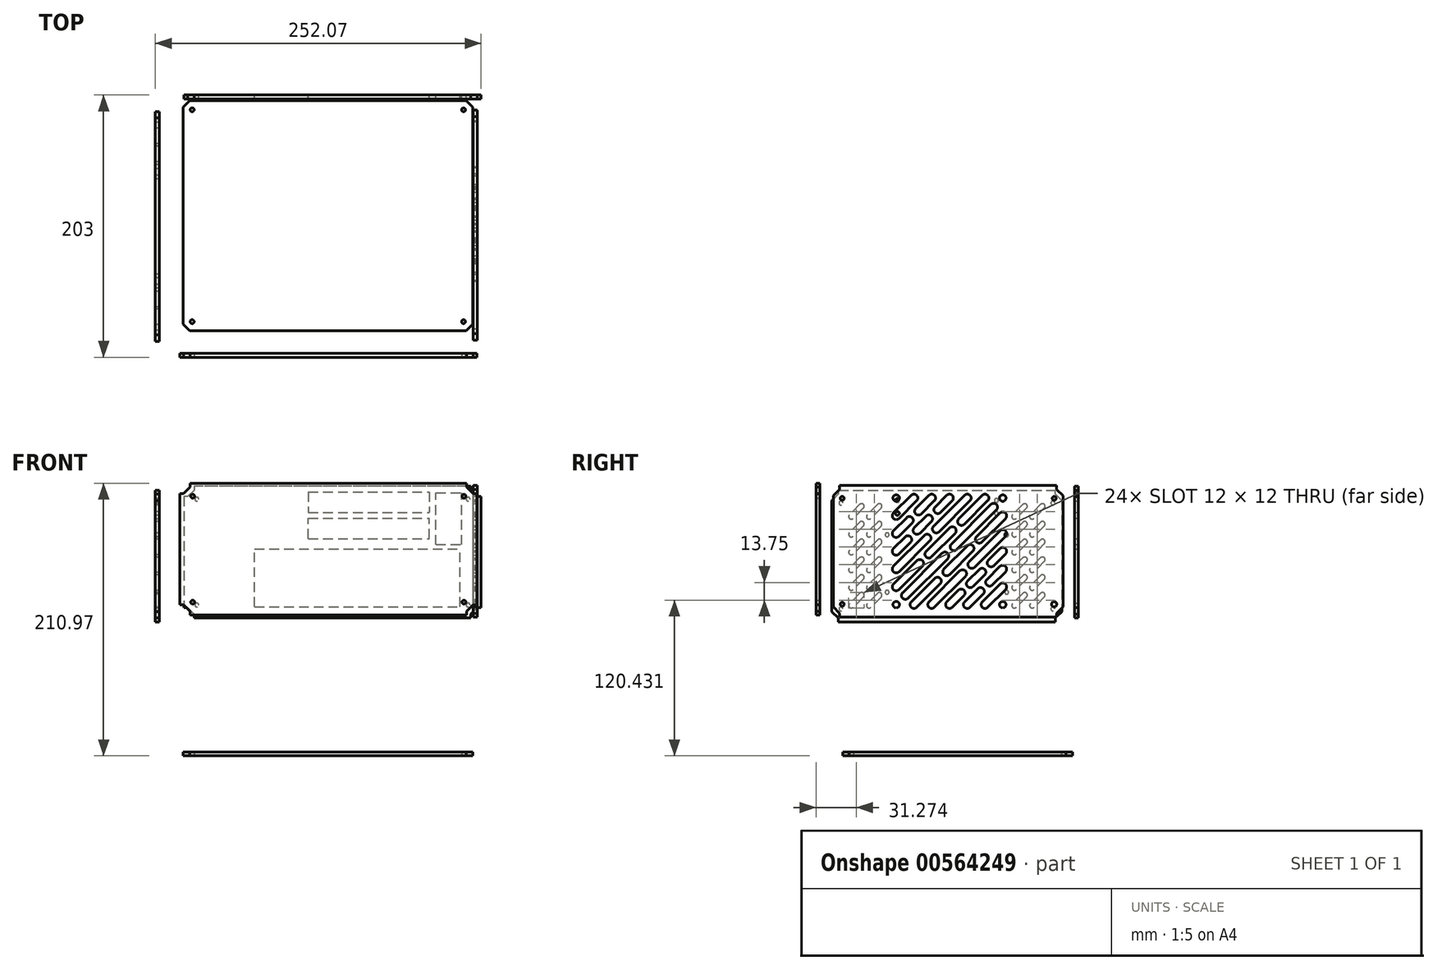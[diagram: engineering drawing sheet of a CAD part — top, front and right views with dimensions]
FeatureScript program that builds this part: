
annotation { "Feature Type Name" : "Feature", "Feature Type Description" : "" }
export const myFeature = defineFeature(function(context is Context, id is Id, definition is map)
    precondition{}
    {
        {
            var Q0;
            Q0=qCreatedBy(makeId("Front.planeOp"),FACE);
            cPlane(context, id + "F0", {"entities" : qUnion([Q0]), "cplaneType" : CPlaneType.OFFSET, "offset" : 80 * mm, "width" : 150 * mm, "height" : 150 * mm});
        }
        {
            var Q0;
            Q0=qCreatedBy(id+"F0.planeOp",FACE);
            var sketch = newSketch(context, id + "F1", { "sketchPlane" : qUnion([Q0])});
            skLineSegment(sketch, "E0.bottom", {"start": v(-107.2, 58.97) * mm, "end": v(122.8, 58.97) * mm});
            skLineSegment(sketch, "E0.top", {"start": v(-107.2, -43.03) * mm, "end": v(122.8, -43.03) * mm});
            skLineSegment(sketch, "E0.left", {"start": v(-107.2, 58.97) * mm, "end": v(-107.2, -43.03) * mm});
            skLineSegment(sketch, "E0.right", {"start": v(122.8, 58.97) * mm, "end": v(122.8, -43.03) * mm});
            skLineSegment(sketch, "E1", {"start": v(114.8, 58.97) * mm, "end": v(114.8, 55.97) * mm});
            skLineSegment(sketch, "E2", {"start": v(114.8, 55.97) * mm, "end": v(119.8, 50.97) * mm});
            skLineSegment(sketch, "E3", {"start": v(119.8, 50.97) * mm, "end": v(122.8, 50.97) * mm});
            skLineSegment(sketch, "E4", {"start": v(122.8, -35.03) * mm, "end": v(119.8, -35.03) * mm});
            skLineSegment(sketch, "E5", {"start": v(119.8, -35.03) * mm, "end": v(114.8, -40.03) * mm});
            skLineSegment(sketch, "E6", {"start": v(114.8, -40.03) * mm, "end": v(114.8, -43.03) * mm});
            skLineSegment(sketch, "E7", {"start": v(-107.2, -35.03) * mm, "end": v(-104.2, -35.03) * mm});
            skLineSegment(sketch, "E8", {"start": v(-104.2, -35.03) * mm, "end": v(-99.2, -40.03) * mm});
            skLineSegment(sketch, "E9", {"start": v(-99.2, -40.03) * mm, "end": v(-99.2, -43.03) * mm});
            skLineSegment(sketch, "E10", {"start": v(-107.2, 50.97) * mm, "end": v(-104.2, 50.97) * mm});
            skLineSegment(sketch, "E11", {"start": v(-104.2, 50.97) * mm, "end": v(-99.2, 55.97) * mm});
            skLineSegment(sketch, "E12", {"start": v(-99.2, 55.97) * mm, "end": v(-99.2, 58.97) * mm});
            skLineSegment(sketch, "E13", {"start": v(-107.2, 48.97) * mm, "end": v(-97.2, 48.97) * mm, "construction": true});
            skCircle(sketch, "E14", {"center": v(-97.2, 48.97) * mm, "radius": 1.5 * mm});
            skLineSegment(sketch, "E15", {"start": v(-107.2, -33.03) * mm, "end": v(-97.2, -33.03) * mm, "construction": true});
            skLineSegment(sketch, "E16", {"start": v(122.8, 48.97) * mm, "end": v(112.8, 48.97) * mm, "construction": true});
            skLineSegment(sketch, "E17", {"start": v(122.8, -33.03) * mm, "end": v(112.8, -33.03) * mm, "construction": true});
            skCircle(sketch, "E18", {"center": v(112.8, -33.03) * mm, "radius": 1.5 * mm});
            skCircle(sketch, "E19", {"center": v(112.8, 48.97) * mm, "radius": 1.5 * mm});
            skCircle(sketch, "E20", {"center": v(-97.2, -33.03) * mm, "radius": 1.5 * mm});
            skSolve(sketch);
        }
        {
            var Q0;
            {var subQ2=sQuery(id+"F1.wireOp",EDGE,"E1");Q0=makeQuery(id+"F1.imprint","IMPRINT",FACE,{"disambiguationData":[TD([[makeQuery(id+"F1.imprint","IMPRINT",EDGE,{"derivedFrom":subQ2}),-1.0]])]});}
            extrude(context, id + "F2", {"entities" : qUnion([Q0]), "depth" : 3 * mm, "offsetDistance" : 25 * mm});
        }
        {
            var Q0;
            Q0=qCreatedBy(makeId("Right.planeOp"),FACE);
            cPlane(context, id + "F3", {"entities" : qUnion([Q0]), "cplaneType" : CPlaneType.OFFSET, "offset" : 120 * mm, "width" : 150 * mm, "height" : 150 * mm});
        }
        {
            var Q0;
            Q0=qCreatedBy(id+"F3.planeOp",FACE);
            var sketch = newSketch(context, id + "F4", { "sketchPlane" : qUnion([Q0])});
            skLineSegment(sketch, "E21.bottom", {"start": v(-69.71, 57.33) * mm, "end": v(108.29, 57.33) * mm});
            skLineSegment(sketch, "E21.top", {"start": v(-69.71, -44.67) * mm, "end": v(108.29, -44.67) * mm});
            skLineSegment(sketch, "E21.left", {"start": v(-69.71, 57.33) * mm, "end": v(-69.71, -44.67) * mm});
            skLineSegment(sketch, "E21.right", {"start": v(108.29, 57.33) * mm, "end": v(108.29, -44.67) * mm});
            skLineSegment(sketch, "E22", {"start": v(-64.71, 57.33) * mm, "end": v(-64.71, 54.33) * mm});
            skLineSegment(sketch, "E23", {"start": v(-64.71, 54.33) * mm, "end": v(-69.71, 49.33) * mm});
            skLineSegment(sketch, "E24", {"start": v(-69.71, -36.67) * mm, "end": v(-64.71, -41.67) * mm});
            skLineSegment(sketch, "E25", {"start": v(-64.71, -41.67) * mm, "end": v(-64.71, -44.67) * mm});
            skLineSegment(sketch, "E26", {"start": v(103.29, 57.33) * mm, "end": v(103.29, 54.33) * mm});
            skLineSegment(sketch, "E27", {"start": v(103.29, 54.33) * mm, "end": v(108.29, 49.33) * mm});
            skLineSegment(sketch, "E28", {"start": v(108.29, -36.67) * mm, "end": v(103.29, -41.67) * mm});
            skLineSegment(sketch, "E29", {"start": v(103.29, -41.67) * mm, "end": v(103.29, -44.67) * mm});
            skLineSegment(sketch, "E30", {"start": v(-69.71, 47.33) * mm, "end": v(-62.71, 47.33) * mm, "construction": true});
            skCircle(sketch, "E31", {"center": v(-62.71, 47.33) * mm, "radius": 1.5 * mm});
            skLineSegment(sketch, "E32", {"start": v(-69.71, -34.67) * mm, "end": v(-62.71, -34.67) * mm, "construction": true});
            skCircle(sketch, "E33", {"center": v(-62.71, -34.67) * mm, "radius": 1.5 * mm});
            skLineSegment(sketch, "E34", {"start": v(108.29, -34.67) * mm, "end": v(101.29, -34.67) * mm, "construction": true});
            skCircle(sketch, "E35", {"center": v(101.29, -34.67) * mm, "radius": 2.05 * mm});
            skLineSegment(sketch, "E36", {"start": v(108.29, 47.33) * mm, "end": v(101.29, 47.33) * mm, "construction": true});
            skCircle(sketch, "E37", {"center": v(101.29, 47.33) * mm, "radius": 1.5 * mm});
            skSolve(sketch);
        }
        {
            var Q0;
            {var subQ4=sQuery(id+"F4.wireOp",EDGE,"E22");Q0=makeQuery(id+"F4.imprint","IMPRINT",FACE,{"disambiguationData":[TD([[makeQuery(id+"F4.imprint","IMPRINT",EDGE,{"derivedFrom":subQ4}),1.0]])]});}
            extrude(context, id + "F5", {"entities" : qUnion([Q0]), "depth" : 3 * mm, "offsetDistance" : 25 * mm});
        }
        {
            var Q0;
            Q0=qCreatedBy(makeId("Front.planeOp"),FACE);
            cPlane(context, id + "F6", {"entities" : qUnion([Q0]), "cplaneType" : CPlaneType.OFFSET, "offset" : 120 * mm, "oppositeDirection" : true, "width" : 150 * mm, "height" : 150 * mm});
        }
        {
            var Q0;
            Q0=qCreatedBy(id+"F6.planeOp",FACE);
            var sketch = newSketch(context, id + "F7", { "sketchPlane" : qUnion([Q0])});
            skLineSegment(sketch, "E38.bottom", {"start": v(126.07, 56.7) * mm, "end": v(-103.93, 56.7) * mm});
            skLineSegment(sketch, "E38.top", {"start": v(126.07, -45.3) * mm, "end": v(-103.93, -45.3) * mm});
            skLineSegment(sketch, "E38.left", {"start": v(126.07, 56.7) * mm, "end": v(126.07, -45.3) * mm});
            skLineSegment(sketch, "E38.right", {"start": v(-103.93, 56.7) * mm, "end": v(-103.93, -45.3) * mm});
            skLineSegment(sketch, "E39", {"start": v(126.07, 48.7) * mm, "end": v(123.07, 48.7) * mm});
            skLineSegment(sketch, "E40", {"start": v(123.07, 48.7) * mm, "end": v(118.07, 53.7) * mm});
            skLineSegment(sketch, "E41", {"start": v(118.07, 53.7) * mm, "end": v(118.07, 56.7) * mm});
            skLineSegment(sketch, "E42", {"start": v(-95.93, 56.7) * mm, "end": v(-95.93, 53.7) * mm});
            skLineSegment(sketch, "E43", {"start": v(-95.93, 53.7) * mm, "end": v(-100.93, 48.7) * mm});
            skLineSegment(sketch, "E44", {"start": v(-100.93, 48.7) * mm, "end": v(-103.93, 48.7) * mm});
            skLineSegment(sketch, "E45", {"start": v(-95.93, -45.3) * mm, "end": v(-95.93, -42.3) * mm});
            skLineSegment(sketch, "E46", {"start": v(-95.93, -42.3) * mm, "end": v(-100.93, -37.3) * mm});
            skLineSegment(sketch, "E47", {"start": v(-100.93, -37.3) * mm, "end": v(-103.93, -37.3) * mm});
            skLineSegment(sketch, "E48", {"start": v(126.07, -37.3) * mm, "end": v(123.07, -37.3) * mm});
            skLineSegment(sketch, "E49", {"start": v(123.07, -37.3) * mm, "end": v(118.07, -42.3) * mm});
            skLineSegment(sketch, "E50", {"start": v(118.07, -42.3) * mm, "end": v(118.07, -45.3) * mm});
            skLineSegment(sketch, "E51", {"start": v(-103.93, 46.7) * mm, "end": v(-93.93, 46.7) * mm, "construction": true});
            skCircle(sketch, "E52", {"center": v(-93.93, 46.7) * mm, "radius": 1.5 * mm});
            skLineSegment(sketch, "E53", {"start": v(-103.93, -35.3) * mm, "end": v(-93.93, -35.3) * mm, "construction": true});
            skCircle(sketch, "E54", {"center": v(-93.93, -35.3) * mm, "radius": 1.5 * mm});
            skLineSegment(sketch, "E55", {"start": v(126.07, 46.7) * mm, "end": v(116.07, 46.7) * mm, "construction": true});
            skCircle(sketch, "E56", {"center": v(116.07, 46.7) * mm, "radius": 1.5 * mm});
            skLineSegment(sketch, "E57", {"start": v(126.07, -35.3) * mm, "end": v(116.07, -35.3) * mm, "construction": true});
            skCircle(sketch, "E58", {"center": v(116.07, -35.3) * mm, "radius": 1.5 * mm});
            skSolve(sketch);
        }
        {
            var Q0;
            {var subQ2=sQuery(id+"F7.wireOp",EDGE,"E39");Q0=makeQuery(id+"F7.imprint","IMPRINT",FACE,{"disambiguationData":[TD([[makeQuery(id+"F7.imprint","IMPRINT",EDGE,{"derivedFrom":subQ2}),1.0]])]});}
            extrude(context, id + "F8", {"entities" : qUnion([Q0]), "depth" : 3 * mm, "offsetDistance" : 25 * mm});
        }
        {
            var Q0;
            Q0=makeQuery(id+"F8.opExtrude","CAP_FACE",FACE,{"disambiguationData":[OSD([sQuery(id+"F7.wireOp",EDGE,"E38.bottom"),sQuery(id+"F7.wireOp",EDGE,"E38.top"),sQuery(id+"F7.wireOp",EDGE,"E38.left"),sQuery(id+"F7.wireOp",EDGE,"E38.right")])],"isStart":true});
            var sketch = newSketch(context, id + "F9", { "sketchPlane" : qUnion([Q0])});
            skLineSegment(sketch, "E59", {"start": v(-107.07, -34.3) * mm, "end": v(62.93, -34.3) * mm, "construction": true});
            skLineSegment(sketch, "E60", {"start": v(-107.07, -34.3) * mm, "end": v(-107.07, -45.3) * mm, "construction": true});
            skLineSegment(sketch, "E61.bottom", {"start": v(-109.67, 8.1) * mm, "end": v(49.33, 8.1) * mm});
            skLineSegment(sketch, "E61.top", {"start": v(-109.67, -36.6) * mm, "end": v(49.33, -36.6) * mm});
            skLineSegment(sketch, "E61.left", {"start": v(-109.67, 8.1) * mm, "end": v(-109.67, -36.6) * mm});
            skLineSegment(sketch, "E61.right", {"start": v(49.33, 8.1) * mm, "end": v(49.33, -36.6) * mm});
            skLineSegment(sketch, "E62.bottom", {"start": v(-86.07, 32) * mm, "end": v(7.63, 32) * mm});
            skLineSegment(sketch, "E62.top", {"start": v(-86.07, 16.1) * mm, "end": v(7.63, 16.1) * mm});
            skLineSegment(sketch, "E62.left", {"start": v(-86.07, 32) * mm, "end": v(-86.07, 16.1) * mm});
            skLineSegment(sketch, "E62.right", {"start": v(7.63, 32) * mm, "end": v(7.63, 16.1) * mm});
            skLineSegment(sketch, "E63", {"start": v(-86.07, 32) * mm, "end": v(-86.07, 36.4) * mm, "construction": true});
            skLineSegment(sketch, "E64.bottom", {"start": v(-86.07, 36.4) * mm, "end": v(7.63, 36.4) * mm});
            skLineSegment(sketch, "E64.top", {"start": v(-86.07, 52.3) * mm, "end": v(7.63, 52.3) * mm});
            skLineSegment(sketch, "E64.left", {"start": v(-86.07, 36.4) * mm, "end": v(-86.07, 52.3) * mm});
            skLineSegment(sketch, "E64.right", {"start": v(7.63, 36.4) * mm, "end": v(7.63, 52.3) * mm});
            skLineSegment(sketch, "E65.bottom", {"start": v(-111.07, 51.6) * mm, "end": v(-91.07, 51.6) * mm});
            skLineSegment(sketch, "E65.top", {"start": v(-111.07, 11.6) * mm, "end": v(-91.07, 11.6) * mm});
            skLineSegment(sketch, "E65.left", {"start": v(-111.07, 51.6) * mm, "end": v(-111.07, 11.6) * mm});
            skLineSegment(sketch, "E65.right", {"start": v(-91.07, 51.6) * mm, "end": v(-91.07, 11.6) * mm});
            skLineSegment(sketch, "E66", {"start": v(-86.07, 16.1) * mm, "end": v(-91.07, 16.1) * mm, "construction": true});
            skSolve(sketch);
        }
        {
            var Q0;
            Q0 = qSketchRegion(id + "F9", true);
            extrude(context, id + "F10", {"entities" : qUnion([Q0]), "operationType" : NewBodyOperationType.REMOVE, "oppositeDirection" : true, "depth" : 25 * mm, "offsetDistance" : 25 * mm});
        }
        {
            var Q0;
            Q0=makeQuery(id+"F5.opExtrude","CAP_FACE",FACE,{"disambiguationData":[OSD([sQuery(id+"F4.wireOp",EDGE,"E21.bottom"),sQuery(id+"F4.wireOp",EDGE,"E21.top"),sQuery(id+"F4.wireOp",EDGE,"E21.left"),sQuery(id+"F4.wireOp",EDGE,"E21.right")])],"isStart":false});
            var sketch = newSketch(context, id + "F11", { "sketchPlane" : qUnion([Q0])});
            skLineSegment(sketch, "E67.bottom", {"start": v(-20.96, 47.58) * mm, "end": v(61.54, 47.58) * mm, "construction": true});
            skLineSegment(sketch, "E67.top", {"start": v(-20.96, -34.92) * mm, "end": v(61.54, -34.92) * mm, "construction": true});
            skLineSegment(sketch, "E67.left", {"start": v(-20.96, 47.58) * mm, "end": v(-20.96, -34.92) * mm, "construction": true});
            skLineSegment(sketch, "E67.right", {"start": v(61.54, 47.58) * mm, "end": v(61.54, -34.92) * mm, "construction": true});
            skLineSegment(sketch, "E68", {"start": v(-20.96, 33.83) * mm, "end": v(-7.21, 47.58) * mm, "construction": true});
            skLineSegment(sketch, "E69", {"start": v(-20.96, 20.08) * mm, "end": v(-10.75, 30.3) * mm, "construction": true});
            skLineSegment(sketch, "E70", {"start": v(-20.96, 6.33) * mm, "end": v(-11.93, 15.36) * mm, "construction": true});
            skLineSegment(sketch, "E71", {"start": v(-20.96, -7.42) * mm, "end": v(3, 16.54) * mm, "construction": true});
            skLineSegment(sketch, "E72", {"start": v(-20.96, -21.17) * mm, "end": v(-2.76, -2.97) * mm, "construction": true});
            skLineSegment(sketch, "E73", {"start": v(-20.96, -34.92) * mm, "end": v(-13.9, -27.85) * mm, "construction": true});
            skArc(sketch, "E74.0.startCap", {"start": v(-18.84, 31.7) * mm, "mid": v(-23.08, 31.7) * mm, "end": v(-23.08, 35.95) * mm});
            skArc(sketch, "E74.0.endCap", {"start": v(-9.33, 49.7) * mm, "mid": v(-5.1, 49.7) * mm, "end": v(-5.1, 45.46) * mm});
            skLineSegment(sketch, "E74.0.left", {"start": v(-23.08, 35.95) * mm, "end": v(-9.33, 49.7) * mm});
            skLineSegment(sketch, "E74.0.right", {"start": v(-18.84, 31.7) * mm, "end": v(-5.1, 45.46) * mm});
            skLineSegment(sketch, "E75", {"start": v(-10.75, 30.3) * mm, "end": v(-3.68, 37.36) * mm, "construction": true});
            skLineSegment(sketch, "E76", {"start": v(-3.68, 37.36) * mm, "end": v(6.54, 47.58) * mm, "construction": true});
            skLineSegment(sketch, "E77", {"start": v(-20.96, -34.92) * mm, "end": v(-20.96, -44.67) * mm, "construction": true});
            skArc(sketch, "E78.0.startCap", {"start": v(-18.84, 17.96) * mm, "mid": v(-23.08, 17.96) * mm, "end": v(-23.08, 22.2) * mm});
            skArc(sketch, "E78.0.endCap", {"start": v(-12.87, 32.41) * mm, "mid": v(-8.63, 32.41) * mm, "end": v(-8.63, 28.17) * mm});
            skLineSegment(sketch, "E78.0.left", {"start": v(-23.08, 22.2) * mm, "end": v(-12.87, 32.41) * mm});
            skLineSegment(sketch, "E78.0.right", {"start": v(-18.84, 17.96) * mm, "end": v(-8.63, 28.17) * mm});
            skArc(sketch, "E78.1.startCap", {"start": v(-1.56, 35.24) * mm, "mid": v(-5.8, 35.24) * mm, "end": v(-5.8, 39.48) * mm});
            skArc(sketch, "E78.1.endCap", {"start": v(4.42, 49.7) * mm, "mid": v(8.66, 49.7) * mm, "end": v(8.66, 45.46) * mm});
            skLineSegment(sketch, "E78.1.left", {"start": v(-5.8, 39.48) * mm, "end": v(4.42, 49.7) * mm});
            skLineSegment(sketch, "E78.1.right", {"start": v(-1.56, 35.24) * mm, "end": v(8.66, 45.46) * mm});
            skLineSegment(sketch, "E79", {"start": v(-11.93, 15.36) * mm, "end": v(-4.86, 22.43) * mm, "construction": true});
            skLineSegment(sketch, "E80", {"start": v(-4.86, 22.43) * mm, "end": v(4.18, 31.47) * mm, "construction": true});
            skLineSegment(sketch, "E81", {"start": v(4.18, 31.47) * mm, "end": v(11.25, 38.54) * mm, "construction": true});
            skLineSegment(sketch, "E82", {"start": v(11.25, 38.54) * mm, "end": v(20.29, 47.58) * mm, "construction": true});
            skArc(sketch, "E83.0.startCap", {"start": v(-18.84, 4.2) * mm, "mid": v(-23.08, 4.2) * mm, "end": v(-23.08, 8.45) * mm});
            skArc(sketch, "E83.0.endCap", {"start": v(-14.05, 17.48) * mm, "mid": v(-9.8, 17.48) * mm, "end": v(-9.8, 13.24) * mm});
            skLineSegment(sketch, "E83.0.left", {"start": v(-23.08, 8.45) * mm, "end": v(-14.05, 17.48) * mm});
            skLineSegment(sketch, "E83.0.right", {"start": v(-18.84, 4.2) * mm, "end": v(-9.8, 13.24) * mm});
            skArc(sketch, "E83.1.startCap", {"start": v(-2.74, 20.31) * mm, "mid": v(-6.98, 20.31) * mm, "end": v(-6.98, 24.56) * mm});
            skArc(sketch, "E83.1.endCap", {"start": v(2.06, 33.6) * mm, "mid": v(6.3, 33.6) * mm, "end": v(6.3, 29.35) * mm});
            skLineSegment(sketch, "E83.1.left", {"start": v(-6.98, 24.56) * mm, "end": v(2.06, 33.6) * mm});
            skLineSegment(sketch, "E83.1.right", {"start": v(-2.74, 20.31) * mm, "end": v(6.3, 29.35) * mm});
            skArc(sketch, "E83.2.startCap", {"start": v(13.37, 36.42) * mm, "mid": v(9.13, 36.42) * mm, "end": v(9.13, 40.66) * mm});
            skArc(sketch, "E83.2.endCap", {"start": v(18.17, 49.7) * mm, "mid": v(22.4, 49.7) * mm, "end": v(22.4, 45.46) * mm});
            skLineSegment(sketch, "E83.2.left", {"start": v(9.13, 40.66) * mm, "end": v(18.17, 49.7) * mm});
            skLineSegment(sketch, "E83.2.right", {"start": v(13.37, 36.42) * mm, "end": v(22.4, 45.46) * mm});
            skLineSegment(sketch, "E84", {"start": v(3, 16.54) * mm, "end": v(10.07, 23.61) * mm, "construction": true});
            skLineSegment(sketch, "E85", {"start": v(10.07, 23.61) * mm, "end": v(34.04, 47.58) * mm, "construction": true});
            skArc(sketch, "E86.0.startCap", {"start": v(-18.84, -9.54) * mm, "mid": v(-23.08, -9.54) * mm, "end": v(-23.08, -5.3) * mm});
            skArc(sketch, "E86.0.endCap", {"start": v(0.88, 18.66) * mm, "mid": v(5.12, 18.66) * mm, "end": v(5.12, 14.42) * mm});
            skLineSegment(sketch, "E86.0.left", {"start": v(-23.08, -5.3) * mm, "end": v(0.88, 18.66) * mm});
            skLineSegment(sketch, "E86.0.right", {"start": v(-18.84, -9.54) * mm, "end": v(5.12, 14.42) * mm});
            skArc(sketch, "E87.0.startCap", {"start": v(12.2, 21.5) * mm, "mid": v(7.95, 21.5) * mm, "end": v(7.95, 25.73) * mm});
            skArc(sketch, "E87.0.endCap", {"start": v(31.92, 49.7) * mm, "mid": v(36.16, 49.7) * mm, "end": v(36.16, 45.46) * mm});
            skLineSegment(sketch, "E87.0.left", {"start": v(7.95, 25.73) * mm, "end": v(31.92, 49.7) * mm});
            skLineSegment(sketch, "E87.0.right", {"start": v(12.2, 21.5) * mm, "end": v(36.16, 45.46) * mm});
            skLineSegment(sketch, "E88", {"start": v(-2.76, -2.97) * mm, "end": v(4.31, 4.1) * mm, "construction": true});
            skLineSegment(sketch, "E89", {"start": v(4.31, 4.1) * mm, "end": v(22.51, 22.3) * mm, "construction": true});
            skLineSegment(sketch, "E90", {"start": v(22.51, 22.3) * mm, "end": v(29.58, 29.37) * mm, "construction": true});
            skLineSegment(sketch, "E91", {"start": v(29.58, 29.37) * mm, "end": v(47.79, 47.58) * mm, "construction": true});
            skArc(sketch, "E92.0.startCap", {"start": v(-18.84, -23.3) * mm, "mid": v(-23.08, -23.3) * mm, "end": v(-23.08, -19.05) * mm});
            skArc(sketch, "E92.0.endCap", {"start": v(-4.88, -0.85) * mm, "mid": v(-0.64, -0.85) * mm, "end": v(-0.64, -5.1) * mm});
            skLineSegment(sketch, "E92.0.left", {"start": v(-23.08, -19.05) * mm, "end": v(-4.88, -0.85) * mm});
            skLineSegment(sketch, "E92.0.right", {"start": v(-18.84, -23.3) * mm, "end": v(-0.64, -5.1) * mm});
            skArc(sketch, "E92.1.startCap", {"start": v(6.43, 1.98) * mm, "mid": v(2.19, 1.98) * mm, "end": v(2.19, 6.22) * mm});
            skArc(sketch, "E92.1.endCap", {"start": v(20.4, 24.42) * mm, "mid": v(24.63, 24.42) * mm, "end": v(24.63, 20.18) * mm});
            skLineSegment(sketch, "E92.1.left", {"start": v(2.19, 6.22) * mm, "end": v(20.4, 24.42) * mm});
            skLineSegment(sketch, "E92.1.right", {"start": v(6.43, 1.98) * mm, "end": v(24.63, 20.18) * mm});
            skArc(sketch, "E92.2.startCap", {"start": v(31.7, 27.25) * mm, "mid": v(27.46, 27.25) * mm, "end": v(27.46, 31.5) * mm});
            skArc(sketch, "E92.2.endCap", {"start": v(45.67, 49.7) * mm, "mid": v(49.9, 49.7) * mm, "end": v(49.9, 45.46) * mm});
            skLineSegment(sketch, "E92.2.left", {"start": v(27.46, 31.5) * mm, "end": v(45.67, 49.7) * mm});
            skLineSegment(sketch, "E92.2.right", {"start": v(31.7, 27.25) * mm, "end": v(49.9, 45.46) * mm});
            skLineSegment(sketch, "E93", {"start": v(-13.9, -27.85) * mm, "end": v(16.75, 2.8) * mm, "construction": true});
            skLineSegment(sketch, "E94", {"start": v(54.47, 40.5) * mm, "end": v(61.54, 47.58) * mm, "construction": true});
            skLineSegment(sketch, "E95", {"start": v(16.75, 2.8) * mm, "end": v(23.82, 9.86) * mm, "construction": true});
            skLineSegment(sketch, "E96", {"start": v(23.82, 9.86) * mm, "end": v(54.47, 40.5) * mm, "construction": true});
            skArc(sketch, "E97.0.startCap", {"start": v(-11.77, -29.97) * mm, "mid": v(-16.01, -29.97) * mm, "end": v(-16.01, -25.73) * mm});
            skArc(sketch, "E97.0.endCap", {"start": v(14.63, 4.91) * mm, "mid": v(18.87, 4.91) * mm, "end": v(18.87, 0.67) * mm});
            skLineSegment(sketch, "E97.0.left", {"start": v(-16.01, -25.73) * mm, "end": v(14.63, 4.91) * mm});
            skLineSegment(sketch, "E97.0.right", {"start": v(-11.77, -29.97) * mm, "end": v(18.87, 0.67) * mm});
            skArc(sketch, "E97.1.startCap", {"start": v(25.94, 7.74) * mm, "mid": v(21.7, 7.74) * mm, "end": v(21.7, 11.98) * mm});
            skArc(sketch, "E97.1.endCap", {"start": v(52.34, 42.63) * mm, "mid": v(56.59, 42.63) * mm, "end": v(56.59, 38.38) * mm});
            skLineSegment(sketch, "E97.1.left", {"start": v(21.7, 11.98) * mm, "end": v(52.34, 42.63) * mm});
            skLineSegment(sketch, "E97.1.right", {"start": v(25.94, 7.74) * mm, "end": v(56.59, 38.38) * mm});
            skLineSegment(sketch, "E98", {"start": v(61.54, 33.83) * mm, "end": v(43.33, 15.62) * mm, "construction": true});
            skLineSegment(sketch, "E99", {"start": v(6.54, -34.92) * mm, "end": v(30.5, -10.96) * mm, "construction": true});
            skLineSegment(sketch, "E100", {"start": v(20.29, -34.92) * mm, "end": v(29.32, -25.89) * mm, "construction": true});
            skLineSegment(sketch, "E101", {"start": v(34.04, -34.92) * mm, "end": v(44.25, -24.7) * mm, "construction": true});
            skLineSegment(sketch, "E102", {"start": v(47.79, -34.92) * mm, "end": v(61.54, -21.17) * mm, "construction": true});
            skLineSegment(sketch, "E103", {"start": v(10.99, -16.72) * mm, "end": v(-7.21, -34.92) * mm, "construction": true});
            skLineSegment(sketch, "E104", {"start": v(18.06, -9.65) * mm, "end": v(10.99, -16.72) * mm, "construction": true});
            skLineSegment(sketch, "E105", {"start": v(43.33, 15.62) * mm, "end": v(36.26, 8.55) * mm, "construction": true});
            skLineSegment(sketch, "E106", {"start": v(36.26, 8.55) * mm, "end": v(18.06, -9.65) * mm, "construction": true});
            skArc(sketch, "E107.0.startCap", {"start": v(8.87, -14.6) * mm, "mid": v(13.11, -14.6) * mm, "end": v(13.11, -18.84) * mm});
            skArc(sketch, "E107.0.endCap", {"start": v(-5.1, -37.04) * mm, "mid": v(-9.33, -37.04) * mm, "end": v(-9.33, -32.8) * mm});
            skLineSegment(sketch, "E107.0.left", {"start": v(13.11, -18.84) * mm, "end": v(-5.1, -37.04) * mm});
            skLineSegment(sketch, "E107.0.right", {"start": v(8.87, -14.6) * mm, "end": v(-9.33, -32.8) * mm});
            skArc(sketch, "E107.1.startCap", {"start": v(34.14, 10.67) * mm, "mid": v(38.38, 10.67) * mm, "end": v(38.38, 6.43) * mm});
            skArc(sketch, "E107.1.endCap", {"start": v(20.18, -11.77) * mm, "mid": v(15.94, -11.77) * mm, "end": v(15.94, -7.53) * mm});
            skLineSegment(sketch, "E107.1.left", {"start": v(38.38, 6.43) * mm, "end": v(20.18, -11.77) * mm});
            skLineSegment(sketch, "E107.1.right", {"start": v(34.14, 10.67) * mm, "end": v(15.94, -7.53) * mm});
            skArc(sketch, "E107.2.startCap", {"start": v(59.42, 35.95) * mm, "mid": v(63.66, 35.95) * mm, "end": v(63.66, 31.7) * mm});
            skArc(sketch, "E107.2.endCap", {"start": v(45.46, 13.5) * mm, "mid": v(41.21, 13.5) * mm, "end": v(41.21, 17.75) * mm});
            skLineSegment(sketch, "E107.2.left", {"start": v(63.66, 31.7) * mm, "end": v(45.46, 13.5) * mm});
            skLineSegment(sketch, "E107.2.right", {"start": v(59.42, 35.95) * mm, "end": v(41.21, 17.75) * mm});
            skLineSegment(sketch, "E108", {"start": v(30.5, -10.96) * mm, "end": v(37.57, -3.89) * mm, "construction": true});
            skLineSegment(sketch, "E109", {"start": v(37.57, -3.89) * mm, "end": v(61.54, 20.08) * mm, "construction": true});
            skArc(sketch, "E110.0.startCap", {"start": v(8.66, -37.04) * mm, "mid": v(4.42, -37.04) * mm, "end": v(4.42, -32.8) * mm});
            skArc(sketch, "E110.0.endCap", {"start": v(28.38, -8.84) * mm, "mid": v(32.62, -8.84) * mm, "end": v(32.62, -13.08) * mm});
            skLineSegment(sketch, "E110.0.left", {"start": v(4.42, -32.8) * mm, "end": v(28.38, -8.84) * mm});
            skLineSegment(sketch, "E110.0.right", {"start": v(8.66, -37.04) * mm, "end": v(32.62, -13.08) * mm});
            skArc(sketch, "E110.1.startCap", {"start": v(39.7, -6) * mm, "mid": v(35.45, -6) * mm, "end": v(35.45, -1.77) * mm});
            skArc(sketch, "E110.1.endCap", {"start": v(59.42, 22.2) * mm, "mid": v(63.66, 22.2) * mm, "end": v(63.66, 17.96) * mm});
            skLineSegment(sketch, "E110.1.left", {"start": v(35.45, -1.77) * mm, "end": v(59.42, 22.2) * mm});
            skLineSegment(sketch, "E110.1.right", {"start": v(39.7, -6) * mm, "end": v(63.66, 17.96) * mm});
            skLineSegment(sketch, "E111", {"start": v(29.32, -25.89) * mm, "end": v(36.4, -18.82) * mm, "construction": true});
            skLineSegment(sketch, "E112", {"start": v(45.43, -9.78) * mm, "end": v(52.5, -2.7) * mm, "construction": true});
            skLineSegment(sketch, "E113", {"start": v(36.4, -18.82) * mm, "end": v(45.43, -9.78) * mm, "construction": true});
            skLineSegment(sketch, "E114", {"start": v(52.5, -2.7) * mm, "end": v(61.54, 6.33) * mm, "construction": true});
            skArc(sketch, "E115.0.startCap", {"start": v(22.4, -37.04) * mm, "mid": v(18.17, -37.04) * mm, "end": v(18.17, -32.8) * mm});
            skArc(sketch, "E115.0.endCap", {"start": v(27.2, -23.77) * mm, "mid": v(31.44, -23.77) * mm, "end": v(31.44, -28) * mm});
            skLineSegment(sketch, "E115.0.left", {"start": v(18.17, -32.8) * mm, "end": v(27.2, -23.77) * mm});
            skLineSegment(sketch, "E115.0.right", {"start": v(22.4, -37.04) * mm, "end": v(31.44, -28) * mm});
            skArc(sketch, "E115.1.startCap", {"start": v(38.51, -20.94) * mm, "mid": v(34.27, -20.94) * mm, "end": v(34.27, -16.7) * mm});
            skArc(sketch, "E115.1.endCap", {"start": v(43.3, -7.66) * mm, "mid": v(47.55, -7.66) * mm, "end": v(47.55, -11.9) * mm});
            skLineSegment(sketch, "E115.1.left", {"start": v(34.27, -16.7) * mm, "end": v(43.3, -7.66) * mm});
            skLineSegment(sketch, "E115.1.right", {"start": v(38.51, -20.94) * mm, "end": v(47.55, -11.9) * mm});
            skArc(sketch, "E115.2.startCap", {"start": v(54.62, -4.83) * mm, "mid": v(50.38, -4.83) * mm, "end": v(50.38, -0.59) * mm});
            skArc(sketch, "E115.2.endCap", {"start": v(59.42, 8.45) * mm, "mid": v(63.66, 8.45) * mm, "end": v(63.66, 4.2) * mm});
            skLineSegment(sketch, "E115.2.left", {"start": v(50.38, -0.59) * mm, "end": v(59.42, 8.45) * mm});
            skLineSegment(sketch, "E115.2.right", {"start": v(54.62, -4.83) * mm, "end": v(63.66, 4.2) * mm});
            skLineSegment(sketch, "E116", {"start": v(44.25, -24.7) * mm, "end": v(51.32, -17.64) * mm, "construction": true});
            skLineSegment(sketch, "E117", {"start": v(51.32, -17.64) * mm, "end": v(61.54, -7.42) * mm, "construction": true});
            skArc(sketch, "E118.0.startCap", {"start": v(36.16, -37.04) * mm, "mid": v(31.92, -37.04) * mm, "end": v(31.92, -32.8) * mm});
            skArc(sketch, "E118.0.endCap", {"start": v(42.13, -22.59) * mm, "mid": v(46.37, -22.59) * mm, "end": v(46.37, -26.83) * mm});
            skLineSegment(sketch, "E118.0.left", {"start": v(31.92, -32.8) * mm, "end": v(42.13, -22.59) * mm});
            skLineSegment(sketch, "E118.0.right", {"start": v(36.16, -37.04) * mm, "end": v(46.37, -26.83) * mm});
            skArc(sketch, "E118.1.startCap", {"start": v(53.44, -19.76) * mm, "mid": v(49.2, -19.76) * mm, "end": v(49.2, -15.52) * mm});
            skArc(sketch, "E118.1.endCap", {"start": v(59.42, -5.3) * mm, "mid": v(63.66, -5.3) * mm, "end": v(63.66, -9.54) * mm});
            skLineSegment(sketch, "E118.1.left", {"start": v(49.2, -15.52) * mm, "end": v(59.42, -5.3) * mm});
            skLineSegment(sketch, "E118.1.right", {"start": v(53.44, -19.76) * mm, "end": v(63.66, -9.54) * mm});
            skArc(sketch, "E119.0.startCap", {"start": v(49.9, -37.04) * mm, "mid": v(45.67, -37.04) * mm, "end": v(45.67, -32.8) * mm});
            skArc(sketch, "E119.0.endCap", {"start": v(59.42, -19.05) * mm, "mid": v(63.66, -19.05) * mm, "end": v(63.66, -23.3) * mm});
            skLineSegment(sketch, "E119.0.left", {"start": v(45.67, -32.8) * mm, "end": v(59.42, -19.05) * mm});
            skLineSegment(sketch, "E119.0.right", {"start": v(49.9, -37.04) * mm, "end": v(63.66, -23.3) * mm});
            skCircle(sketch, "E120", {"center": v(61.54, 47.58) * mm, "radius": 2.5 * mm});
            skCircle(sketch, "E121", {"center": v(-20.96, 47.58) * mm, "radius": 2.5 * mm});
            skCircle(sketch, "E122", {"center": v(61.54, -34.92) * mm, "radius": 2.5 * mm});
            skCircle(sketch, "E123", {"center": v(-20.96, -34.92) * mm, "radius": 2.5 * mm});
            skLineSegment(sketch, "E124", {"start": v(-20.96, -34.92) * mm, "end": v(-69.71, -34.92) * mm, "construction": true});
            skSolve(sketch);
        }
        {
            var Q0;
            Q0 = qSketchRegion(id + "F11", true);
            extrude(context, id + "F12", {"entities" : qUnion([Q0]), "operationType" : NewBodyOperationType.REMOVE, "oppositeDirection" : true, "depth" : 25 * mm, "offsetDistance" : 25 * mm});
        }
        {
            var Q0;
            Q0=qCreatedBy(makeId("Right.planeOp"),FACE);
            cPlane(context, id + "F13", {"entities" : qUnion([Q0]), "cplaneType" : CPlaneType.OFFSET, "offset" : 126 * mm, "oppositeDirection" : true, "width" : 150 * mm, "height" : 150 * mm});
        }
        {
            var Q0;
            Q0=qCreatedBy(id+"F13.planeOp",FACE);
            var sketch = newSketch(context, id + "F14", { "sketchPlane" : qUnion([Q0])});
            skLineSegment(sketch, "E125.bottom", {"start": v(-70.73, 53.68) * mm, "end": v(107.27, 53.68) * mm});
            skLineSegment(sketch, "E125.top", {"start": v(-70.73, -48.32) * mm, "end": v(107.27, -48.32) * mm});
            skLineSegment(sketch, "E125.left", {"start": v(-70.73, 53.68) * mm, "end": v(-70.73, -48.32) * mm});
            skLineSegment(sketch, "E125.right", {"start": v(107.27, 53.68) * mm, "end": v(107.27, -48.32) * mm});
            skLineSegment(sketch, "E126", {"start": v(107.27, 45.68) * mm, "end": v(102.27, 50.68) * mm});
            skLineSegment(sketch, "E127", {"start": v(102.27, 50.68) * mm, "end": v(102.27, 53.68) * mm});
            skLineSegment(sketch, "E128", {"start": v(-65.73, 53.68) * mm, "end": v(-65.73, 50.68) * mm});
            skLineSegment(sketch, "E129", {"start": v(-65.73, 50.68) * mm, "end": v(-70.73, 45.68) * mm});
            skLineSegment(sketch, "E130", {"start": v(-65.73, -48.32) * mm, "end": v(-65.73, -45.32) * mm});
            skLineSegment(sketch, "E131", {"start": v(-65.73, -45.32) * mm, "end": v(-70.73, -40.32) * mm});
            skLineSegment(sketch, "E132", {"start": v(107.27, -40.32) * mm, "end": v(102.27, -45.32) * mm});
            skLineSegment(sketch, "E133", {"start": v(102.27, -45.32) * mm, "end": v(102.27, -48.32) * mm});
            skLineSegment(sketch, "E134", {"start": v(100.27, -48.32) * mm, "end": v(100.27, -38.32) * mm, "construction": true});
            skCircle(sketch, "E135", {"center": v(100.27, -38.32) * mm, "radius": 1.5 * mm});
            skLineSegment(sketch, "E136", {"start": v(100.27, 53.68) * mm, "end": v(100.27, 43.68) * mm, "construction": true});
            skCircle(sketch, "E137", {"center": v(100.27, 43.68) * mm, "radius": 1.5 * mm});
            skLineSegment(sketch, "E138", {"start": v(-63.73, 53.68) * mm, "end": v(-63.73, 43.68) * mm, "construction": true});
            skCircle(sketch, "E139", {"center": v(-63.73, 43.68) * mm, "radius": 1.5 * mm});
            skLineSegment(sketch, "E140", {"start": v(-63.73, -48.32) * mm, "end": v(-63.73, -38.32) * mm, "construction": true});
            skCircle(sketch, "E141", {"center": v(-63.73, -38.32) * mm, "radius": 1.5 * mm});
            skSolve(sketch);
        }
        {
            var Q0;
            {var subQ4=sQuery(id+"F14.wireOp",EDGE,"E126");Q0=makeQuery(id+"F14.imprint","IMPRINT",FACE,{"disambiguationData":[TD([[makeQuery(id+"F14.imprint","IMPRINT",EDGE,{"derivedFrom":subQ4}),1.0]])]});}
            extrude(context, id + "F15", {"entities" : qUnion([Q0]), "depth" : 3 * mm, "offsetDistance" : 25 * mm});
        }
        {
            var Q0;
            Q0=qCreatedBy(makeId("Top.planeOp"),FACE);
            cPlane(context, id + "F16", {"entities" : qUnion([Q0]), "cplaneType" : CPlaneType.OFFSET, "offset" : 152 * mm, "oppositeDirection" : true, "width" : 150 * mm, "height" : 150 * mm});
        }
        {
            var Q0;
            Q0=qCreatedBy(id+"F16.planeOp",FACE);
            var sketch = newSketch(context, id + "F17", { "sketchPlane" : qUnion([Q0])});
            skLineSegment(sketch, "E142.bottom", {"start": v(-104.54, -62.39) * mm, "end": v(119.46, -62.39) * mm});
            skLineSegment(sketch, "E142.top", {"start": v(-104.54, 115.61) * mm, "end": v(119.46, 115.61) * mm});
            skLineSegment(sketch, "E142.left", {"start": v(-104.54, -62.39) * mm, "end": v(-104.54, 115.61) * mm});
            skLineSegment(sketch, "E142.right", {"start": v(119.46, -62.39) * mm, "end": v(119.46, 115.61) * mm});
            skLineSegment(sketch, "E143", {"start": v(-104.54, -57.39) * mm, "end": v(-99.54, -62.39) * mm});
            skLineSegment(sketch, "E144", {"start": v(114.46, -62.39) * mm, "end": v(119.46, -57.39) * mm});
            skLineSegment(sketch, "E145", {"start": v(119.46, 110.61) * mm, "end": v(114.46, 115.61) * mm});
            skLineSegment(sketch, "E146", {"start": v(-104.54, 110.61) * mm, "end": v(-99.54, 115.61) * mm});
            skLineSegment(sketch, "E147", {"start": v(112.46, -62.39) * mm, "end": v(112.46, -55.39) * mm, "construction": true});
            skCircle(sketch, "E148", {"center": v(112.46, -55.39) * mm, "radius": 1.5 * mm});
            skLineSegment(sketch, "E149", {"start": v(112.46, 115.61) * mm, "end": v(112.46, 108.61) * mm, "construction": true});
            skCircle(sketch, "E150", {"center": v(112.46, 108.61) * mm, "radius": 1.5 * mm});
            skLineSegment(sketch, "E151", {"start": v(-97.54, 115.61) * mm, "end": v(-97.54, 108.61) * mm, "construction": true});
            skCircle(sketch, "E152", {"center": v(-97.54, 108.61) * mm, "radius": 1.5 * mm});
            skLineSegment(sketch, "E153", {"start": v(-97.54, -62.39) * mm, "end": v(-97.54, -55.39) * mm, "construction": true});
            skCircle(sketch, "E154", {"center": v(-97.54, -55.39) * mm, "radius": 1.5 * mm});
            skSolve(sketch);
        }
        {
            var Q0;
            {var subQ3=sQuery(id+"F17.wireOp",EDGE,"E143");Q0=makeQuery(id+"F17.imprint","IMPRINT",FACE,{"disambiguationData":[TD([[makeQuery(id+"F17.imprint","IMPRINT",EDGE,{"derivedFrom":subQ3}),1.0]])]});}
            extrude(context, id + "F18", {"entities" : qUnion([Q0]), "depth" : 3 * mm, "offsetDistance" : 25 * mm});
        }
        {
            var Q0;
            Q0=makeQuery(id+"F15.opExtrude","CAP_FACE",FACE,{"disambiguationData":[OSD([sQuery(id+"F14.wireOp",EDGE,"E125.bottom"),sQuery(id+"F14.wireOp",EDGE,"E125.top"),sQuery(id+"F14.wireOp",EDGE,"E125.left"),sQuery(id+"F14.wireOp",EDGE,"E125.right"),sQuery(id+"F14.wireOp",EDGE,"E126"),sQuery(id+"F14.wireOp",EDGE,"E127"),sQuery(id+"F14.wireOp",EDGE,"E128"),sQuery(id+"F14.wireOp",EDGE,"E129"),sQuery(id+"F14.wireOp",EDGE,"E130"),sQuery(id+"F14.wireOp",EDGE,"E131"),sQuery(id+"F14.wireOp",EDGE,"E132"),sQuery(id+"F14.wireOp",EDGE,"E133"),sQuery(id+"F14.wireOp",EDGE,"E135"),sQuery(id+"F14.wireOp",EDGE,"E137"),sQuery(id+"F14.wireOp",EDGE,"E139"),sQuery(id+"F14.wireOp",EDGE,"E141")])],"isStart":true});
            var sketch = newSketch(context, id + "F19", { "sketchPlane" : qUnion([Q0])});
            skLineSegment(sketch, "E155", {"start": v(55.73, -48.32) * mm, "end": v(55.73, -35.57) * mm, "construction": true});
            skLineSegment(sketch, "E156", {"start": v(55.73, -35.57) * mm, "end": v(47.73, -27.57) * mm, "construction": true});
            skArc(sketch, "E157.0.startCap", {"start": v(57.14, -34.15) * mm, "mid": v(57.14, -36.98) * mm, "end": v(54.31, -36.98) * mm});
            skArc(sketch, "E157.0.endCap", {"start": v(46.31, -28.98) * mm, "mid": v(46.31, -26.15) * mm, "end": v(49.14, -26.15) * mm});
            skLineSegment(sketch, "E157.0.left", {"start": v(54.31, -36.98) * mm, "end": v(46.31, -28.98) * mm});
            skLineSegment(sketch, "E157.0.right", {"start": v(57.14, -34.15) * mm, "end": v(49.14, -26.15) * mm});
            skArc(sketch, "E158.0.1.0", {"start": v(46.31, -15.23) * mm, "mid": v(46.31, -12.4) * mm, "end": v(49.14, -12.4) * mm});
            skLineSegment(sketch, "E158.0.1.1", {"start": v(54.31, -23.23) * mm, "end": v(46.31, -15.23) * mm});
            skLineSegment(sketch, "E158.0.1.2", {"start": v(57.14, -20.4) * mm, "end": v(49.14, -12.4) * mm});
            skArc(sketch, "E158.0.1.3", {"start": v(57.14, -20.4) * mm, "mid": v(57.14, -23.23) * mm, "end": v(54.31, -23.23) * mm});
            skLineSegment(sketch, "E158.0.1.4", {"start": v(55.73, -21.82) * mm, "end": v(47.73, -13.82) * mm, "construction": true});
            skArc(sketch, "E158.0.2.0", {"start": v(46.31, -1.48) * mm, "mid": v(46.31, 1.35) * mm, "end": v(49.14, 1.35) * mm});
            skLineSegment(sketch, "E158.0.2.1", {"start": v(54.31, -9.48) * mm, "end": v(46.31, -1.48) * mm});
            skLineSegment(sketch, "E158.0.2.2", {"start": v(57.14, -6.65) * mm, "end": v(49.14, 1.35) * mm});
            skArc(sketch, "E158.0.2.3", {"start": v(57.14, -6.65) * mm, "mid": v(57.14, -9.48) * mm, "end": v(54.31, -9.48) * mm});
            skLineSegment(sketch, "E158.0.2.4", {"start": v(55.73, -8.07) * mm, "end": v(47.73, -0.07) * mm, "construction": true});
            skArc(sketch, "E158.0.3.0", {"start": v(46.31, 12.27) * mm, "mid": v(46.31, 15.1) * mm, "end": v(49.14, 15.1) * mm});
            skLineSegment(sketch, "E158.0.3.1", {"start": v(54.31, 4.27) * mm, "end": v(46.31, 12.27) * mm});
            skLineSegment(sketch, "E158.0.3.2", {"start": v(57.14, 7.1) * mm, "end": v(49.14, 15.1) * mm});
            skArc(sketch, "E158.0.3.3", {"start": v(57.14, 7.1) * mm, "mid": v(57.14, 4.27) * mm, "end": v(54.31, 4.27) * mm});
            skLineSegment(sketch, "E158.0.3.4", {"start": v(55.73, 5.68) * mm, "end": v(47.73, 13.68) * mm, "construction": true});
            skArc(sketch, "E158.0.4.0", {"start": v(46.31, 26.02) * mm, "mid": v(46.31, 28.85) * mm, "end": v(49.14, 28.85) * mm});
            skLineSegment(sketch, "E158.0.4.1", {"start": v(54.31, 18.02) * mm, "end": v(46.31, 26.02) * mm});
            skLineSegment(sketch, "E158.0.4.2", {"start": v(57.14, 20.85) * mm, "end": v(49.14, 28.85) * mm});
            skArc(sketch, "E158.0.4.3", {"start": v(57.14, 20.85) * mm, "mid": v(57.14, 18.02) * mm, "end": v(54.31, 18.02) * mm});
            skLineSegment(sketch, "E158.0.4.4", {"start": v(55.73, 19.43) * mm, "end": v(47.73, 27.43) * mm, "construction": true});
            skArc(sketch, "E158.0.5.0", {"start": v(46.31, 39.77) * mm, "mid": v(46.31, 42.6) * mm, "end": v(49.14, 42.6) * mm});
            skLineSegment(sketch, "E158.0.5.1", {"start": v(54.31, 31.77) * mm, "end": v(46.31, 39.77) * mm});
            skLineSegment(sketch, "E158.0.5.2", {"start": v(57.14, 34.6) * mm, "end": v(49.14, 42.6) * mm});
            skArc(sketch, "E158.0.5.3", {"start": v(57.14, 34.6) * mm, "mid": v(57.14, 31.77) * mm, "end": v(54.31, 31.77) * mm});
            skLineSegment(sketch, "E158.0.5.4", {"start": v(55.73, 33.18) * mm, "end": v(47.73, 41.18) * mm, "construction": true});
            skLineSegment(sketch, "E158.direction1", {"start": v(40.56, -36.98) * mm, "end": v(54.31, -36.98) * mm, "construction": true});
            skLineSegment(sketch, "E158.direction2", {"start": v(54.31, -36.98) * mm, "end": v(54.31, -23.23) * mm, "construction": true});
            skArc(sketch, "E159.0.1.0", {"start": v(32.56, -28.98) * mm, "mid": v(32.56, -26.15) * mm, "end": v(35.4, -26.15) * mm});
            skLineSegment(sketch, "E159.4.1.0", {"start": v(40.56, -36.98) * mm, "end": v(32.56, -28.98) * mm});
            skLineSegment(sketch, "E159.7.1.0", {"start": v(43.4, -34.15) * mm, "end": v(35.4, -26.15) * mm});
            skArc(sketch, "E159.10.1.0", {"start": v(43.4, -34.15) * mm, "mid": v(43.4, -36.98) * mm, "end": v(40.56, -36.98) * mm});
            skLineSegment(sketch, "E159.14.1.0", {"start": v(41.98, -35.57) * mm, "end": v(33.98, -27.57) * mm, "construction": true});
            skArc(sketch, "E159.0.1.1", {"start": v(32.56, -15.23) * mm, "mid": v(32.56, -12.4) * mm, "end": v(35.4, -12.4) * mm});
            skLineSegment(sketch, "E159.4.1.1", {"start": v(40.56, -23.23) * mm, "end": v(32.56, -15.23) * mm});
            skLineSegment(sketch, "E159.7.1.1", {"start": v(43.4, -20.4) * mm, "end": v(35.4, -12.4) * mm});
            skArc(sketch, "E159.10.1.1", {"start": v(43.4, -20.4) * mm, "mid": v(43.4, -23.23) * mm, "end": v(40.56, -23.23) * mm});
            skLineSegment(sketch, "E159.14.1.1", {"start": v(41.98, -21.82) * mm, "end": v(33.98, -13.82) * mm, "construction": true});
            skArc(sketch, "E159.0.1.2", {"start": v(32.56, -1.48) * mm, "mid": v(32.56, 1.35) * mm, "end": v(35.4, 1.35) * mm});
            skLineSegment(sketch, "E159.4.1.2", {"start": v(40.56, -9.48) * mm, "end": v(32.56, -1.48) * mm});
            skLineSegment(sketch, "E159.7.1.2", {"start": v(43.4, -6.65) * mm, "end": v(35.4, 1.35) * mm});
            skArc(sketch, "E159.10.1.2", {"start": v(43.4, -6.65) * mm, "mid": v(43.4, -9.48) * mm, "end": v(40.56, -9.48) * mm});
            skLineSegment(sketch, "E159.14.1.2", {"start": v(41.98, -8.07) * mm, "end": v(33.98, -0.07) * mm, "construction": true});
            skArc(sketch, "E159.0.1.3", {"start": v(32.56, 12.27) * mm, "mid": v(32.56, 15.1) * mm, "end": v(35.4, 15.1) * mm});
            skLineSegment(sketch, "E159.4.1.3", {"start": v(40.56, 4.27) * mm, "end": v(32.56, 12.27) * mm});
            skLineSegment(sketch, "E159.7.1.3", {"start": v(43.4, 7.1) * mm, "end": v(35.4, 15.1) * mm});
            skArc(sketch, "E159.10.1.3", {"start": v(43.4, 7.1) * mm, "mid": v(43.4, 4.27) * mm, "end": v(40.56, 4.27) * mm});
            skLineSegment(sketch, "E159.14.1.3", {"start": v(41.98, 5.68) * mm, "end": v(33.98, 13.68) * mm, "construction": true});
            skArc(sketch, "E159.0.1.4", {"start": v(32.56, 26.02) * mm, "mid": v(32.56, 28.85) * mm, "end": v(35.4, 28.85) * mm});
            skLineSegment(sketch, "E159.4.1.4", {"start": v(40.56, 18.02) * mm, "end": v(32.56, 26.02) * mm});
            skLineSegment(sketch, "E159.7.1.4", {"start": v(43.4, 20.85) * mm, "end": v(35.4, 28.85) * mm});
            skArc(sketch, "E159.10.1.4", {"start": v(43.4, 20.85) * mm, "mid": v(43.4, 18.02) * mm, "end": v(40.56, 18.02) * mm});
            skLineSegment(sketch, "E159.14.1.4", {"start": v(41.98, 19.43) * mm, "end": v(33.98, 27.43) * mm, "construction": true});
            skArc(sketch, "E159.0.1.5", {"start": v(32.56, 39.77) * mm, "mid": v(32.56, 42.6) * mm, "end": v(35.4, 42.6) * mm});
            skLineSegment(sketch, "E159.4.1.5", {"start": v(40.56, 31.77) * mm, "end": v(32.56, 39.77) * mm});
            skLineSegment(sketch, "E159.7.1.5", {"start": v(43.4, 34.6) * mm, "end": v(35.4, 42.6) * mm});
            skArc(sketch, "E159.10.1.5", {"start": v(43.4, 34.6) * mm, "mid": v(43.4, 31.77) * mm, "end": v(40.56, 31.77) * mm});
            skLineSegment(sketch, "E159.14.1.5", {"start": v(41.98, 33.18) * mm, "end": v(33.98, 41.18) * mm, "construction": true});
            skLineSegment(sketch, "E160", {"start": v(-84.27, -48.32) * mm, "end": v(-84.27, -35.57) * mm, "construction": true});
            skLineSegment(sketch, "E161", {"start": v(-84.27, -35.57) * mm, "end": v(-92.27, -27.57) * mm, "construction": true});
            skArc(sketch, "E162.0.startCap", {"start": v(-82.86, -34.15) * mm, "mid": v(-82.86, -36.98) * mm, "end": v(-85.69, -36.98) * mm});
            skArc(sketch, "E162.0.endCap", {"start": v(-93.69, -28.98) * mm, "mid": v(-93.69, -26.15) * mm, "end": v(-90.86, -26.15) * mm});
            skLineSegment(sketch, "E162.0.left", {"start": v(-85.69, -36.98) * mm, "end": v(-93.69, -28.98) * mm});
            skLineSegment(sketch, "E162.0.right", {"start": v(-82.86, -34.15) * mm, "end": v(-90.86, -26.15) * mm});
            skLineSegment(sketch, "E163.0.1.0", {"start": v(-85.69, -23.23) * mm, "end": v(-93.69, -15.23) * mm});
            skLineSegment(sketch, "E163.0.1.1", {"start": v(-82.86, -20.4) * mm, "end": v(-90.86, -12.4) * mm});
            skArc(sketch, "E163.0.1.2", {"start": v(-93.69, -15.23) * mm, "mid": v(-93.69, -12.4) * mm, "end": v(-90.86, -12.4) * mm});
            skArc(sketch, "E163.0.1.3", {"start": v(-82.86, -20.4) * mm, "mid": v(-82.86, -23.23) * mm, "end": v(-85.69, -23.23) * mm});
            skLineSegment(sketch, "E163.0.1.4", {"start": v(-84.27, -21.82) * mm, "end": v(-92.27, -13.82) * mm, "construction": true});
            skLineSegment(sketch, "E163.0.2.0", {"start": v(-85.69, -9.48) * mm, "end": v(-93.69, -1.48) * mm});
            skLineSegment(sketch, "E163.0.2.1", {"start": v(-82.86, -6.65) * mm, "end": v(-90.86, 1.35) * mm});
            skArc(sketch, "E163.0.2.2", {"start": v(-93.69, -1.48) * mm, "mid": v(-93.69, 1.35) * mm, "end": v(-90.86, 1.35) * mm});
            skArc(sketch, "E163.0.2.3", {"start": v(-82.86, -6.65) * mm, "mid": v(-82.86, -9.48) * mm, "end": v(-85.69, -9.48) * mm});
            skLineSegment(sketch, "E163.0.2.4", {"start": v(-84.27, -8.07) * mm, "end": v(-92.27, -0.07) * mm, "construction": true});
            skLineSegment(sketch, "E163.0.3.0", {"start": v(-85.69, 4.27) * mm, "end": v(-93.69, 12.27) * mm});
            skLineSegment(sketch, "E163.0.3.1", {"start": v(-82.86, 7.1) * mm, "end": v(-90.86, 15.1) * mm});
            skArc(sketch, "E163.0.3.2", {"start": v(-93.69, 12.27) * mm, "mid": v(-93.69, 15.1) * mm, "end": v(-90.86, 15.1) * mm});
            skArc(sketch, "E163.0.3.3", {"start": v(-82.86, 7.1) * mm, "mid": v(-82.86, 4.27) * mm, "end": v(-85.69, 4.27) * mm});
            skLineSegment(sketch, "E163.0.3.4", {"start": v(-84.27, 5.68) * mm, "end": v(-92.27, 13.68) * mm, "construction": true});
            skLineSegment(sketch, "E163.0.4.0", {"start": v(-85.69, 18.02) * mm, "end": v(-93.69, 26.02) * mm});
            skLineSegment(sketch, "E163.0.4.1", {"start": v(-82.86, 20.85) * mm, "end": v(-90.86, 28.85) * mm});
            skArc(sketch, "E163.0.4.2", {"start": v(-93.69, 26.02) * mm, "mid": v(-93.69, 28.85) * mm, "end": v(-90.86, 28.85) * mm});
            skArc(sketch, "E163.0.4.3", {"start": v(-82.86, 20.85) * mm, "mid": v(-82.86, 18.02) * mm, "end": v(-85.69, 18.02) * mm});
            skLineSegment(sketch, "E163.0.4.4", {"start": v(-84.27, 19.43) * mm, "end": v(-92.27, 27.43) * mm, "construction": true});
            skLineSegment(sketch, "E163.0.5.0", {"start": v(-85.69, 31.77) * mm, "end": v(-93.69, 39.77) * mm});
            skLineSegment(sketch, "E163.0.5.1", {"start": v(-82.86, 34.6) * mm, "end": v(-90.86, 42.6) * mm});
            skArc(sketch, "E163.0.5.2", {"start": v(-93.69, 39.77) * mm, "mid": v(-93.69, 42.6) * mm, "end": v(-90.86, 42.6) * mm});
            skArc(sketch, "E163.0.5.3", {"start": v(-82.86, 34.6) * mm, "mid": v(-82.86, 31.77) * mm, "end": v(-85.69, 31.77) * mm});
            skLineSegment(sketch, "E163.0.5.4", {"start": v(-84.27, 33.18) * mm, "end": v(-92.27, 41.18) * mm, "construction": true});
            skLineSegment(sketch, "E163.1.0.0", {"start": v(-71.94, -36.98) * mm, "end": v(-79.94, -28.98) * mm});
            skLineSegment(sketch, "E163.1.0.1", {"start": v(-69.1, -34.15) * mm, "end": v(-77.1, -26.15) * mm});
            skArc(sketch, "E163.1.0.2", {"start": v(-79.94, -28.98) * mm, "mid": v(-79.94, -26.15) * mm, "end": v(-77.1, -26.15) * mm});
            skArc(sketch, "E163.1.0.3", {"start": v(-69.1, -34.15) * mm, "mid": v(-69.1, -36.98) * mm, "end": v(-71.94, -36.98) * mm});
            skLineSegment(sketch, "E163.1.0.4", {"start": v(-70.52, -35.57) * mm, "end": v(-78.52, -27.57) * mm, "construction": true});
            skLineSegment(sketch, "E163.1.1.0", {"start": v(-71.94, -23.23) * mm, "end": v(-79.94, -15.23) * mm});
            skLineSegment(sketch, "E163.1.1.1", {"start": v(-69.1, -20.4) * mm, "end": v(-77.1, -12.4) * mm});
            skArc(sketch, "E163.1.1.2", {"start": v(-79.94, -15.23) * mm, "mid": v(-79.94, -12.4) * mm, "end": v(-77.1, -12.4) * mm});
            skArc(sketch, "E163.1.1.3", {"start": v(-69.1, -20.4) * mm, "mid": v(-69.1, -23.23) * mm, "end": v(-71.94, -23.23) * mm});
            skLineSegment(sketch, "E163.1.1.4", {"start": v(-70.52, -21.82) * mm, "end": v(-78.52, -13.82) * mm, "construction": true});
            skLineSegment(sketch, "E163.1.2.0", {"start": v(-71.94, -9.48) * mm, "end": v(-79.94, -1.48) * mm});
            skLineSegment(sketch, "E163.1.2.1", {"start": v(-69.1, -6.65) * mm, "end": v(-77.1, 1.35) * mm});
            skArc(sketch, "E163.1.2.2", {"start": v(-79.94, -1.48) * mm, "mid": v(-79.94, 1.35) * mm, "end": v(-77.1, 1.35) * mm});
            skArc(sketch, "E163.1.2.3", {"start": v(-69.1, -6.65) * mm, "mid": v(-69.1, -9.48) * mm, "end": v(-71.94, -9.48) * mm});
            skLineSegment(sketch, "E163.1.2.4", {"start": v(-70.52, -8.07) * mm, "end": v(-78.52, -0.07) * mm, "construction": true});
            skLineSegment(sketch, "E163.1.3.0", {"start": v(-71.94, 4.27) * mm, "end": v(-79.94, 12.27) * mm});
            skLineSegment(sketch, "E163.1.3.1", {"start": v(-69.1, 7.1) * mm, "end": v(-77.1, 15.1) * mm});
            skArc(sketch, "E163.1.3.2", {"start": v(-79.94, 12.27) * mm, "mid": v(-79.94, 15.1) * mm, "end": v(-77.1, 15.1) * mm});
            skArc(sketch, "E163.1.3.3", {"start": v(-69.1, 7.1) * mm, "mid": v(-69.1, 4.27) * mm, "end": v(-71.94, 4.27) * mm});
            skLineSegment(sketch, "E163.1.3.4", {"start": v(-70.52, 5.68) * mm, "end": v(-78.52, 13.68) * mm, "construction": true});
            skLineSegment(sketch, "E163.1.4.0", {"start": v(-71.94, 18.02) * mm, "end": v(-79.94, 26.02) * mm});
            skLineSegment(sketch, "E163.1.4.1", {"start": v(-69.1, 20.85) * mm, "end": v(-77.1, 28.85) * mm});
            skArc(sketch, "E163.1.4.2", {"start": v(-79.94, 26.02) * mm, "mid": v(-79.94, 28.85) * mm, "end": v(-77.1, 28.85) * mm});
            skArc(sketch, "E163.1.4.3", {"start": v(-69.1, 20.85) * mm, "mid": v(-69.1, 18.02) * mm, "end": v(-71.94, 18.02) * mm});
            skLineSegment(sketch, "E163.1.4.4", {"start": v(-70.52, 19.43) * mm, "end": v(-78.52, 27.43) * mm, "construction": true});
            skLineSegment(sketch, "E163.1.5.0", {"start": v(-71.94, 31.77) * mm, "end": v(-79.94, 39.77) * mm});
            skLineSegment(sketch, "E163.1.5.1", {"start": v(-69.1, 34.6) * mm, "end": v(-77.1, 42.6) * mm});
            skArc(sketch, "E163.1.5.2", {"start": v(-79.94, 39.77) * mm, "mid": v(-79.94, 42.6) * mm, "end": v(-77.1, 42.6) * mm});
            skArc(sketch, "E163.1.5.3", {"start": v(-69.1, 34.6) * mm, "mid": v(-69.1, 31.77) * mm, "end": v(-71.94, 31.77) * mm});
            skLineSegment(sketch, "E163.1.5.4", {"start": v(-70.52, 33.18) * mm, "end": v(-78.52, 41.18) * mm, "construction": true});
            skLineSegment(sketch, "E163.direction1", {"start": v(-85.69, -36.98) * mm, "end": v(-71.94, -36.98) * mm, "construction": true});
            skLineSegment(sketch, "E163.direction2", {"start": v(-85.69, -36.98) * mm, "end": v(-85.69, -23.23) * mm, "construction": true});
            skLineSegment(sketch, "E164.bottom", {"start": v(-64.52, 19.13) * mm, "end": v(27.98, 19.13) * mm, "construction": true});
            skLineSegment(sketch, "E164.top", {"start": v(-64.52, -25.32) * mm, "end": v(27.98, -25.32) * mm, "construction": true});
            skLineSegment(sketch, "E164.left", {"start": v(-64.52, 19.13) * mm, "end": v(-64.52, -25.32) * mm, "construction": true});
            skLineSegment(sketch, "E164.right", {"start": v(27.98, 19.13) * mm, "end": v(27.98, -25.32) * mm, "construction": true});
            skLineSegment(sketch, "E165", {"start": v(-18.27, -25.32) * mm, "end": v(-18.27, -48.32) * mm, "construction": true});
            skLineSegment(sketch, "E166", {"start": v(-56.57, 45.68) * mm, "end": v(20.03, 45.68) * mm, "construction": true});
            skCircle(sketch, "E167", {"center": v(-56.57, 45.68) * mm, "radius": 1.5 * mm});
            skCircle(sketch, "E168", {"center": v(20.03, 45.68) * mm, "radius": 1.5 * mm});
            skLineSegment(sketch, "E169", {"start": v(-18.27, 45.68) * mm, "end": v(-18.27, 53.68) * mm, "construction": true});
            skLineSegment(sketch, "E170.0.1.0", {"start": v(-56.57, 35.68) * mm, "end": v(20.03, 35.68) * mm, "construction": true});
            skCircle(sketch, "E170.0.1.1", {"center": v(-56.57, 35.68) * mm, "radius": 1.5 * mm});
            skCircle(sketch, "E170.0.1.2", {"center": v(20.03, 35.68) * mm, "radius": 1.5 * mm});
            skLineSegment(sketch, "E170.direction1", {"start": v(-56.57, 45.68) * mm, "end": v(-32.57, 45.68) * mm, "construction": true});
            skLineSegment(sketch, "E170.direction2", {"start": v(-56.57, 45.68) * mm, "end": v(-56.57, 35.68) * mm, "construction": true});
            skCircle(sketch, "E171", {"center": v(-64.52, 19.13) * mm, "radius": 1.5 * mm});
            skCircle(sketch, "E172", {"center": v(27.98, 19.13) * mm, "radius": 1.5 * mm});
            skCircle(sketch, "E173", {"center": v(27.98, -25.32) * mm, "radius": 1.5 * mm});
            skCircle(sketch, "E174", {"center": v(-64.52, -25.32) * mm, "radius": 1.5 * mm});
            skSolve(sketch);
        }
        {
            var Q0;
            Q0 = qSketchRegion(id + "F19", true);
            extrude(context, id + "F20", {"entities" : qUnion([Q0]), "operationType" : NewBodyOperationType.REMOVE, "oppositeDirection" : true, "depth" : 25 * mm, "offsetDistance" : 25 * mm});
        }
    });
